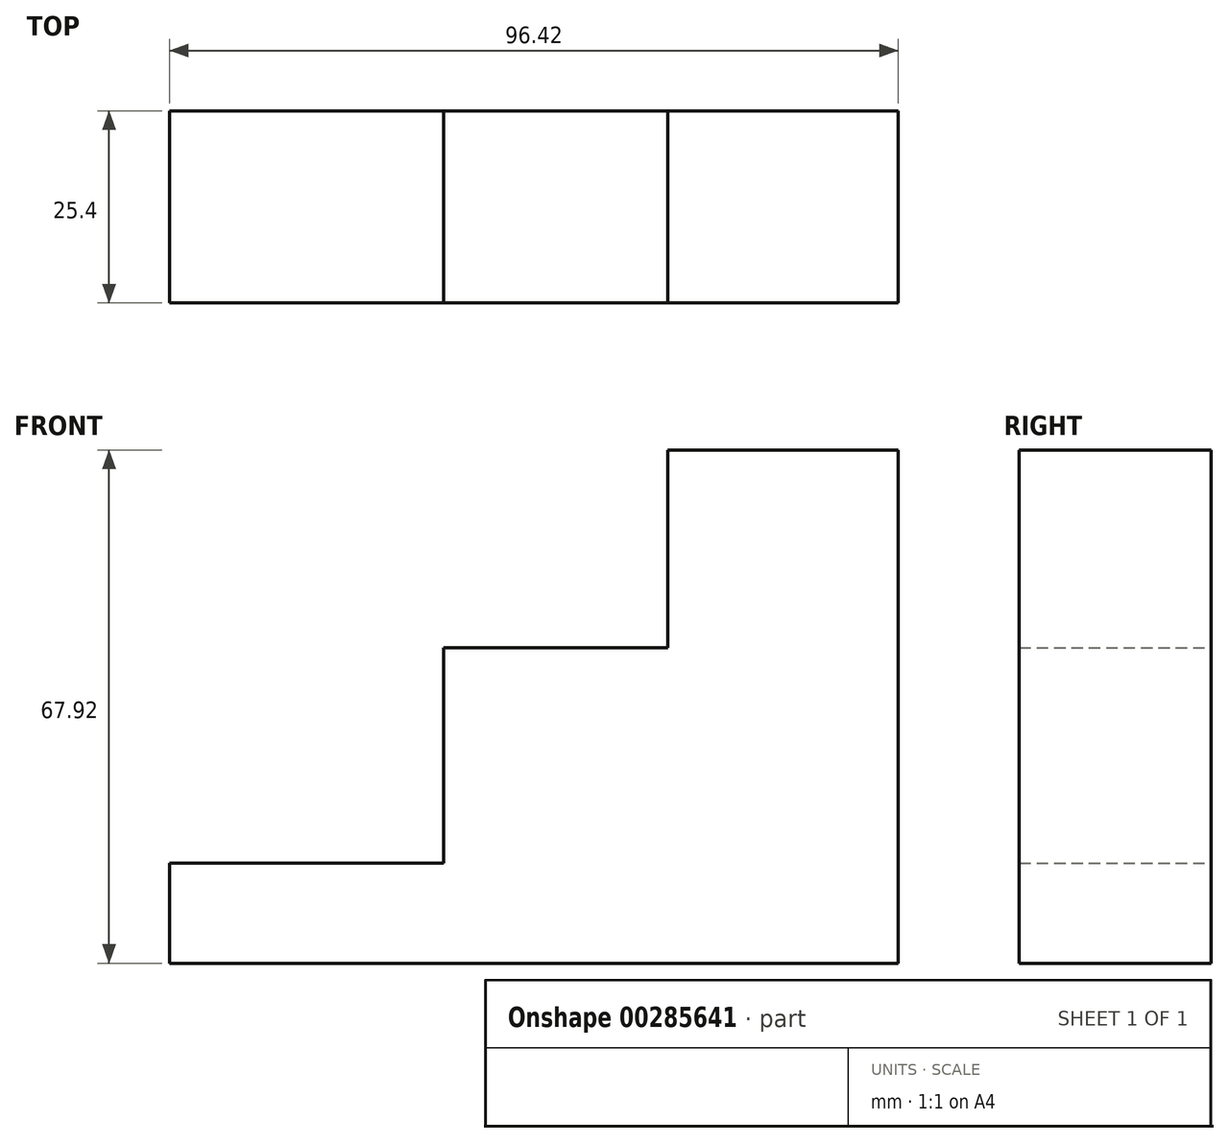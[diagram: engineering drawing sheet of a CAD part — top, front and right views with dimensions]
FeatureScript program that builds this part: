
annotation { "Feature Type Name" : "Feature", "Feature Type Description" : "" }
export const myFeature = defineFeature(function(context is Context, id is Id, definition is map)
    precondition{}
    {
        {
            var Q0;
            Q0=qCreatedBy(makeId("Front.planeOp"),FACE);
            var sketch = newSketch(context, id + "F0", { "sketchPlane" : qUnion([Q0])});
            skLineSegment(sketch, "E0", {"start": v(-65.9, -25.04) * mm, "end": v(-32.52, -25.04) * mm});
            skLineSegment(sketch, "E1", {"start": v(-32.52, -25.04) * mm, "end": v(-32.52, 3.45) * mm});
            skLineSegment(sketch, "E2", {"start": v(-32.52, 3.45) * mm, "end": v(-2.88, 3.45) * mm});
            skLineSegment(sketch, "E3", {"start": v(-2.88, 3.45) * mm, "end": v(-2.88, 29.64) * mm});
            skLineSegment(sketch, "E4", {"start": v(-2.88, 29.64) * mm, "end": v(27.63, 29.64) * mm});
            skLineSegment(sketch, "E5", {"start": v(27.63, 29.64) * mm, "end": v(27.63, -38.28) * mm});
            skLineSegment(sketch, "E6", {"start": v(27.63, -38.28) * mm, "end": v(-68.79, -38.28) * mm});
            skLineSegment(sketch, "E7", {"start": v(-68.79, -38.28) * mm, "end": v(-68.79, -25.04) * mm});
            skLineSegment(sketch, "E8", {"start": v(-68.79, -25.04) * mm, "end": v(-65.9, -25.04) * mm});
            skSolve(sketch);
        }
        {
            var Q0;
            Q0 = qSketchRegion(id + "F0", true);
            extrude(context, id + "F1", {"entities" : qUnion([Q0]), "depth" : 25.4 * mm});
        }
    });
